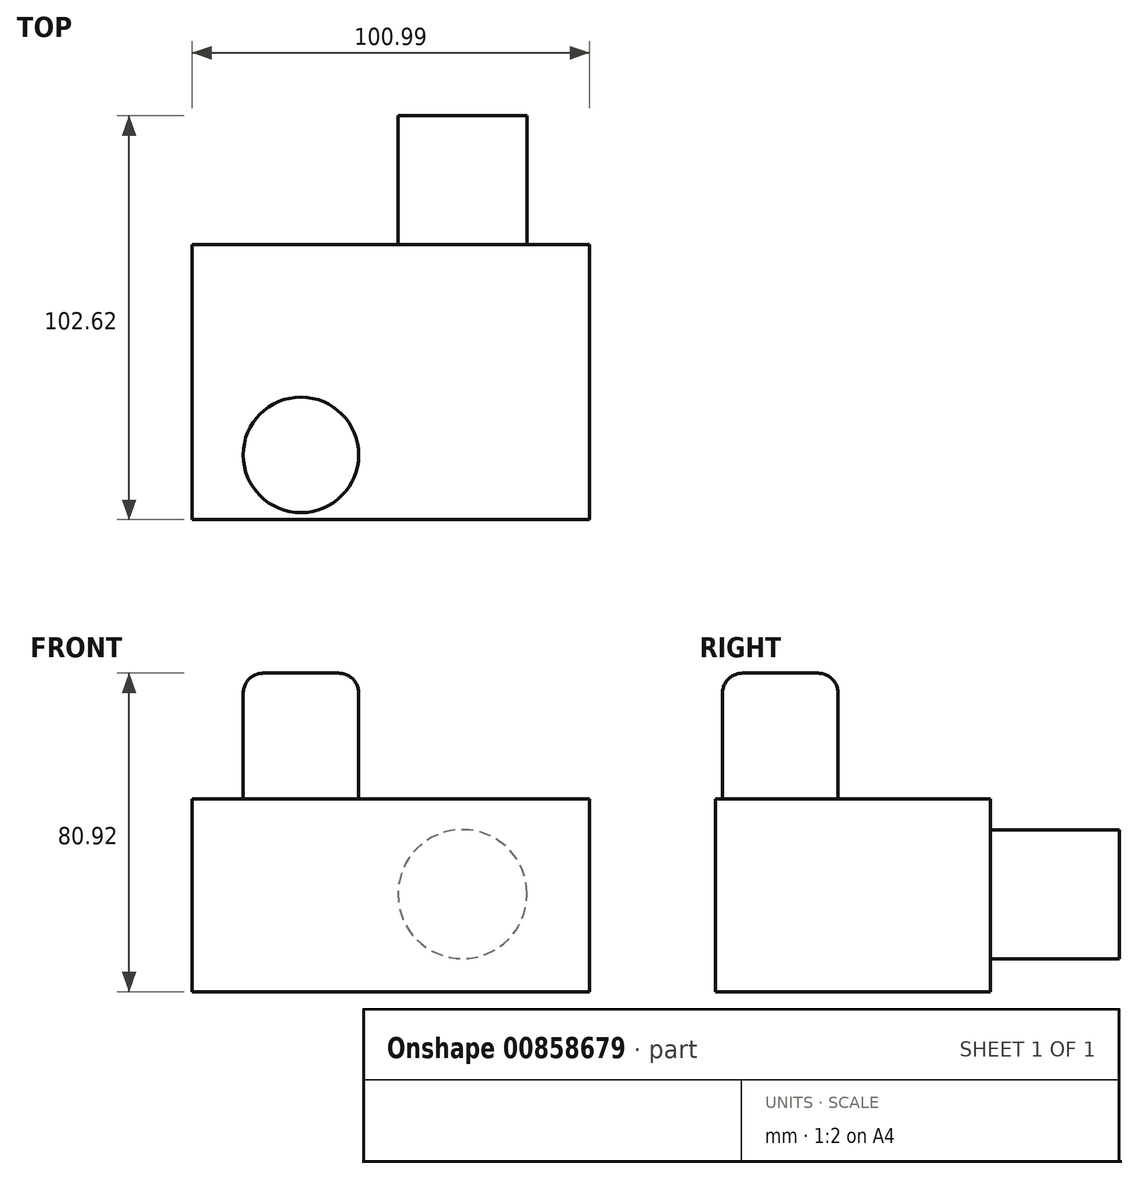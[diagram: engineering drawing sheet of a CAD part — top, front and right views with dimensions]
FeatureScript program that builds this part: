
annotation { "Feature Type Name" : "Feature", "Feature Type Description" : "" }
export const myFeature = defineFeature(function(context is Context, id is Id, definition is map)
    precondition{}
    {
        {
            var Q0;
            Q0=qCreatedBy(makeId("Front.planeOp"),FACE);
            var sketch = newSketch(context, id + "F0", { "sketchPlane" : qUnion([Q0])});
            skLineSegment(sketch, "E0.bottom", {"start": v(-58.47, 56.5) * mm, "end": v(10.77, 56.5) * mm});
            skLineSegment(sketch, "E0.top", {"start": v(-58.47, 7.58) * mm, "end": v(10.77, 7.58) * mm});
            skLineSegment(sketch, "E0.left", {"start": v(-58.47, 56.5) * mm, "end": v(-58.47, 7.58) * mm});
            skLineSegment(sketch, "E0.right", {"start": v(10.77, 56.5) * mm, "end": v(10.77, 7.58) * mm});
            skSolve(sketch);
        }
        {
            var Q0;
            Q0=makeQuery(id+"F0.imprint","IMPRINT",FACE,{"disambiguationData":[TD([[makeQuery(id+"F0.imprint","IMPRINT",EDGE,{"derivedFrom":sQuery(id+"F0.wireOp",EDGE,"E0.bottom")}),-1.0]])]});
            extrude(context, id + "F1", {"entities" : qUnion([Q0]), "depth" : 69.85 * mm, "offsetDistance" : 25.4 * mm});
        }
        {
            var Q0;
            Q0=makeQuery(id+"F1.opExtrude","SWEPT_FACE",FACE,{"disambiguationData":[OSD([sQuery(id+"F0.wireOp",EDGE,"E0.right")])]});
            extrude(context, id + "F2", {"entities" : qUnion([Q0]), "operationType" : NewBodyOperationType.ADD, "depth" : 31.75 * mm, "offsetDistance" : 25.4 * mm});
        }
        {
            var Q0;
            {var subQ0=sQuery(id+"F0.wireOp",EDGE,"E0.bottom");Q0=makeQuery(id+"F2.boolean.opBoolean","MERGE",FACE,{"derivedFrom":[makeQuery(id+"F1.opExtrude","SWEPT_FACE",FACE,{"disambiguationData":[OSD([subQ0])]}),makeQuery(id+"F2.opExtrude","SWEPT_FACE",FACE,{"disambiguationData":[OSD([subQ0,sQuery(id+"F0.wireOp",EDGE,"E0.right")])]})]});}
            var sketch = newSketch(context, id + "F3", { "sketchPlane" : qUnion([Q0])});
            skCircle(sketch, "E1", {"center": v(-38.98, -41.22) * mm, "radius": 14.67 * mm});
            skCircle(sketch, "E2", {"center": v(-30.8, -53.4) * mm, "radius": 14.67 * mm});
            skSolve(sketch);
        }
        {
            var Q0;
            {var subQ0=sQuery(id+"F3.wireOp",EDGE,"E2");var subQ1=sQuery(id+"F3.wireOp",EDGE,"E1");var subQ2=makeQuery(id+"F3.imprint","INTERSECT",VERTEX,{"disambiguationData":[OD(0.0)],"derivedFrom":[subQ1,subQ0]});Q0=makeQuery(id+"F3.imprint","IMPRINT",FACE,{"disambiguationData":[TD([[makeQuery(id+"F3.imprint","IMPRINT",EDGE,{"disambiguationData":[TD([[subQ2,-1.0]])],"derivedFrom":subQ1}),1.0]])]});}
            var Q1;
            {var subQ0=sQuery(id+"F3.wireOp",EDGE,"E2");var subQ1=sQuery(id+"F3.wireOp",EDGE,"E1");var subQ2=makeQuery(id+"F3.imprint","INTERSECT",VERTEX,{"disambiguationData":[OD(0.0)],"derivedFrom":[subQ1,subQ0]});Q1=makeQuery(id+"F3.imprint","IMPRINT",FACE,{"disambiguationData":[TD([[makeQuery(id+"F3.imprint","IMPRINT",EDGE,{"disambiguationData":[TD([[subQ2,-1.0]])],"derivedFrom":subQ1}),-1.0]])]});}
            extrude(context, id + "F4", {"entities" : qUnion([Q0, Q1]), "operationType" : NewBodyOperationType.ADD, "depth" : 32 * mm, "offsetDistance" : 25.4 * mm});
        }
        {
            var Q0;
            Q0=makeQuery(id+"F4.opExtrude","CAP_FACE",FACE,{"disambiguationData":[OSD([sQuery(id+"F3.wireOp",EDGE,"E2")])],"isStart":false});
            var Q1;
            Q1=makeQuery(id+"F4.opExtrude","CAP_EDGE",EDGE,{"disambiguationData":[OSD([sQuery(id+"F3.wireOp",EDGE,"E2")])],"isStart":true});
            fillet(context, id + "F5", {"entities" : qUnion([Q0, Q1]), "radius" : 5.08 * mm, "tangentPropagation" : true, "allowEdgeOverflow" : false});
        }
        {
            var Q0;
            {var subQ0=sQuery(id+"F0.wireOp",EDGE,"E0.right");Q0=makeQuery(id+"F2.boolean.opBoolean","MERGE",FACE,{"derivedFrom":[makeQuery(id+"F1.opExtrude","CAP_FACE",FACE,{"disambiguationData":[OSD([sQuery(id+"F0.wireOp",EDGE,"E0.bottom"),sQuery(id+"F0.wireOp",EDGE,"E0.top"),sQuery(id+"F0.wireOp",EDGE,"E0.left"),subQ0])],"isStart":false}),makeQuery(id+"F2.opExtrude","SWEPT_FACE",FACE,{"disambiguationData":[OSD([subQ0]),TDD([makeQuery(id+"F1.opExtrude","CAP_EDGE",EDGE,{"disambiguationData":[OSD([subQ0])],"isStart":false})])]})]});}
            var sketch = newSketch(context, id + "F6", { "sketchPlane" : qUnion([Q0])});
            skCircle(sketch, "E3", {"center": v(10.25, 32.35) * mm, "radius": 16.39 * mm});
            skSolve(sketch);
        }
        {
            var Q0;
            Q0=makeQuery(id+"F6.imprint","IMPRINT",FACE,{"disambiguationData":[TD([[makeQuery(id+"F6.imprint","IMPRINT",EDGE,{"derivedFrom":sQuery(id+"F6.wireOp",EDGE,"E3")}),1.0]])]});
            extrude(context, id + "F7", {"entities" : qUnion([Q0]), "operationType" : NewBodyOperationType.ADD, "oppositeDirection" : true, "depth" : 102.62 * mm, "offsetDistance" : 25.4 * mm});
        }
    });
